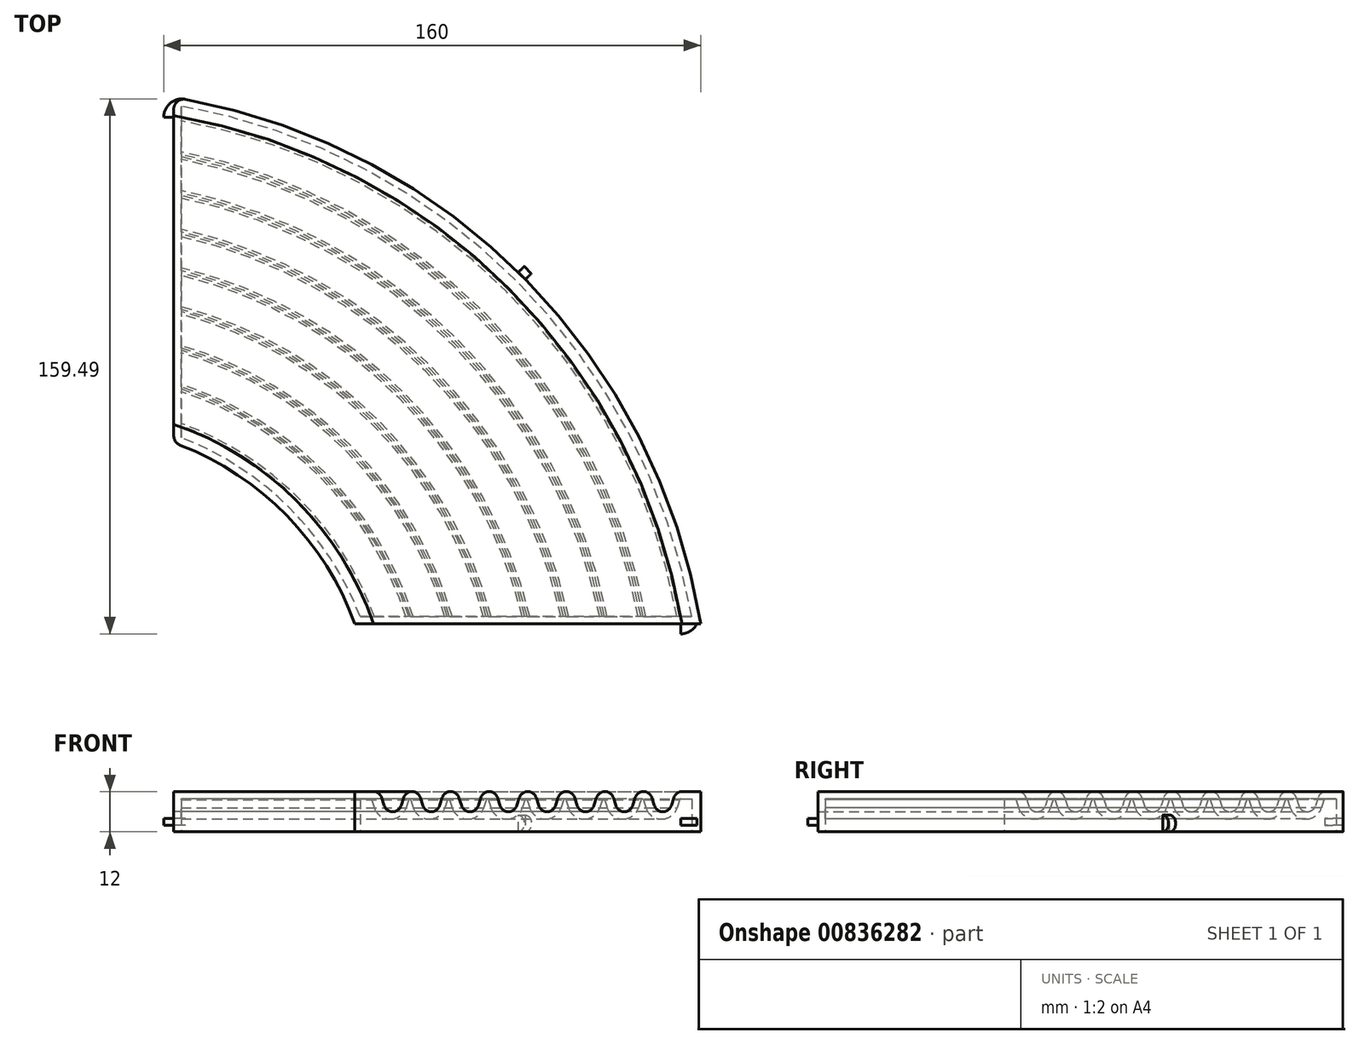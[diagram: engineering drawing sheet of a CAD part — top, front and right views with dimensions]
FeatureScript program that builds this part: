
annotation { "Feature Type Name" : "Feature", "Feature Type Description" : "" }
export const myFeature = defineFeature(function(context is Context, id is Id, definition is map)
    precondition{}
    {
        {
            var Q0;
            Q0=qCreatedBy(makeId("Right.planeOp"),FACE);
            cPlane(context, id + "F0", {"entities" : qUnion([Q0]), "cplaneType" : CPlaneType.OFFSET, "offset" : 31 * mm, "oppositeDirection" : true, "width" : 150 * mm, "height" : 150 * mm});
        }
        {
            var Q0;
            Q0=qCreatedBy(id+"F0.planeOp",FACE);
            var sketch = newSketch(context, id + "F1", { "sketchPlane" : qUnion([Q0])});
            skLineSegment(sketch, "E0", {"start": v(-31, 47.21) * mm, "end": v(-31, -48.38) * mm, "construction": true});
            skSolve(sketch);
        }
        {
            var Q0;
            Q0=qCreatedBy(makeId("Front.planeOp"),FACE);
            var sketch = newSketch(context, id + "F2", { "sketchPlane" : qUnion([Q0])});
            skLineSegment(sketch, "E1", {"start": v(0, 0) * mm, "end": v(54, 0) * mm, "construction": true});
            skLineSegment(sketch, "E2", {"start": v(54, 0) * mm, "end": v(54, 12) * mm});
            skLineSegment(sketch, "E3", {"start": v(54, 12) * mm, "end": v(59.5, 12) * mm});
            skLineSegment(sketch, "E4", {"start": v(59.5, 12) * mm, "end": v(71, 12) * mm, "construction": true});
            skLineSegment(sketch, "E5", {"start": v(65.25, 12) * mm, "end": v(65.25, 6) * mm, "construction": true});
            skLineSegment(sketch, "E6", {"start": v(151.5, 12) * mm, "end": v(157, 12) * mm});
            skLineSegment(sketch, "E7", {"start": v(157, 12) * mm, "end": v(157, 0) * mm});
            skLineSegment(sketch, "E8", {"start": v(157, 0) * mm, "end": v(54, 0) * mm});
            skLineSegment(sketch, "E9", {"start": v(0, 0) * mm, "end": v(0, 12) * mm, "construction": true});
            skLineSegment(sketch, "E10", {"start": v(65.25, 6) * mm, "end": v(71, 6) * mm, "construction": true});
            skArc(sketch, "E11", {"start": v(61.99, 10.19) * mm, "mid": v(61.04, 11.5) * mm, "end": v(59.5, 12) * mm});
            skLineSegment(sketch, "E12", {"start": v(61.99, 10.19) * mm, "end": v(62.76, 7.81) * mm});
            skArc(sketch, "E13", {"start": v(62.76, 7.81) * mm, "mid": v(63.71, 6.5) * mm, "end": v(65.25, 6) * mm});
            skLineSegment(sketch, "E14.MirrorCS", {"start": v(68.51, 10.19) * mm, "end": v(67.74, 7.81) * mm});
            skArc(sketch, "E15.MirrorCS", {"start": v(68.51, 10.19) * mm, "mid": v(69.46, 11.5) * mm, "end": v(71, 12) * mm});
            skArc(sketch, "E16.MirrorCS", {"start": v(67.74, 7.81) * mm, "mid": v(66.79, 6.5) * mm, "end": v(65.25, 6) * mm});
            skLineSegment(sketch, "E17.direction1", {"start": v(59.5, 9.38) * mm, "end": v(71, 9.38) * mm, "construction": true});
            skArc(sketch, "E18.1.0.0", {"start": v(73.49, 10.19) * mm, "mid": v(72.54, 11.5) * mm, "end": v(71, 12) * mm});
            skLineSegment(sketch, "E18.1.0.1", {"start": v(73.49, 10.19) * mm, "end": v(74.26, 7.81) * mm});
            skArc(sketch, "E18.1.0.2", {"start": v(74.26, 7.81) * mm, "mid": v(75.21, 6.5) * mm, "end": v(76.75, 6) * mm});
            skArc(sketch, "E18.1.0.3", {"start": v(79.24, 7.81) * mm, "mid": v(78.29, 6.5) * mm, "end": v(76.75, 6) * mm});
            skLineSegment(sketch, "E18.1.0.4", {"start": v(80.01, 10.19) * mm, "end": v(79.24, 7.81) * mm});
            skArc(sketch, "E18.1.0.5", {"start": v(80.01, 10.19) * mm, "mid": v(80.96, 11.5) * mm, "end": v(82.5, 12) * mm});
            skArc(sketch, "E18.2.0.0", {"start": v(84.99, 10.19) * mm, "mid": v(84.04, 11.5) * mm, "end": v(82.5, 12) * mm});
            skLineSegment(sketch, "E18.2.0.1", {"start": v(84.99, 10.19) * mm, "end": v(85.76, 7.81) * mm});
            skArc(sketch, "E18.2.0.2", {"start": v(85.76, 7.81) * mm, "mid": v(86.71, 6.5) * mm, "end": v(88.25, 6) * mm});
            skArc(sketch, "E18.2.0.3", {"start": v(90.74, 7.81) * mm, "mid": v(89.79, 6.5) * mm, "end": v(88.25, 6) * mm});
            skLineSegment(sketch, "E18.2.0.4", {"start": v(91.51, 10.19) * mm, "end": v(90.74, 7.81) * mm});
            skArc(sketch, "E18.2.0.5", {"start": v(91.51, 10.19) * mm, "mid": v(92.46, 11.5) * mm, "end": v(94, 12) * mm});
            skArc(sketch, "E18.3.0.0", {"start": v(96.49, 10.19) * mm, "mid": v(95.54, 11.5) * mm, "end": v(94, 12) * mm});
            skLineSegment(sketch, "E18.3.0.1", {"start": v(96.49, 10.19) * mm, "end": v(97.26, 7.81) * mm});
            skArc(sketch, "E18.3.0.2", {"start": v(97.26, 7.81) * mm, "mid": v(98.21, 6.5) * mm, "end": v(99.75, 6) * mm});
            skArc(sketch, "E18.3.0.3", {"start": v(102.24, 7.81) * mm, "mid": v(101.29, 6.5) * mm, "end": v(99.75, 6) * mm});
            skLineSegment(sketch, "E18.3.0.4", {"start": v(103.01, 10.19) * mm, "end": v(102.24, 7.81) * mm});
            skArc(sketch, "E18.3.0.5", {"start": v(103.01, 10.19) * mm, "mid": v(103.96, 11.5) * mm, "end": v(105.5, 12) * mm});
            skArc(sketch, "E18.4.0.0", {"start": v(107.99, 10.19) * mm, "mid": v(107.04, 11.5) * mm, "end": v(105.5, 12) * mm});
            skLineSegment(sketch, "E18.4.0.1", {"start": v(107.99, 10.19) * mm, "end": v(108.76, 7.81) * mm});
            skArc(sketch, "E18.4.0.2", {"start": v(108.76, 7.81) * mm, "mid": v(109.71, 6.5) * mm, "end": v(111.25, 6) * mm});
            skArc(sketch, "E18.4.0.3", {"start": v(113.74, 7.81) * mm, "mid": v(112.79, 6.5) * mm, "end": v(111.25, 6) * mm});
            skLineSegment(sketch, "E18.4.0.4", {"start": v(114.51, 10.19) * mm, "end": v(113.74, 7.81) * mm});
            skArc(sketch, "E18.4.0.5", {"start": v(114.51, 10.19) * mm, "mid": v(115.46, 11.5) * mm, "end": v(117, 12) * mm});
            skArc(sketch, "E18.5.0.0", {"start": v(119.49, 10.19) * mm, "mid": v(118.54, 11.5) * mm, "end": v(117, 12) * mm});
            skLineSegment(sketch, "E18.5.0.1", {"start": v(119.49, 10.19) * mm, "end": v(120.26, 7.81) * mm});
            skArc(sketch, "E18.5.0.2", {"start": v(120.26, 7.81) * mm, "mid": v(121.21, 6.5) * mm, "end": v(122.75, 6) * mm});
            skArc(sketch, "E18.5.0.3", {"start": v(125.24, 7.81) * mm, "mid": v(124.29, 6.5) * mm, "end": v(122.75, 6) * mm});
            skLineSegment(sketch, "E18.5.0.4", {"start": v(126.01, 10.19) * mm, "end": v(125.24, 7.81) * mm});
            skArc(sketch, "E18.5.0.5", {"start": v(126.01, 10.19) * mm, "mid": v(126.96, 11.5) * mm, "end": v(128.5, 12) * mm});
            skArc(sketch, "E18.6.0.0", {"start": v(130.99, 10.19) * mm, "mid": v(130.04, 11.5) * mm, "end": v(128.5, 12) * mm});
            skLineSegment(sketch, "E18.6.0.1", {"start": v(130.99, 10.19) * mm, "end": v(131.76, 7.81) * mm});
            skArc(sketch, "E18.6.0.2", {"start": v(131.76, 7.81) * mm, "mid": v(132.71, 6.5) * mm, "end": v(134.25, 6) * mm});
            skArc(sketch, "E18.6.0.3", {"start": v(136.74, 7.81) * mm, "mid": v(135.79, 6.5) * mm, "end": v(134.25, 6) * mm});
            skLineSegment(sketch, "E18.6.0.4", {"start": v(137.51, 10.19) * mm, "end": v(136.74, 7.81) * mm});
            skArc(sketch, "E18.6.0.5", {"start": v(137.51, 10.19) * mm, "mid": v(138.46, 11.5) * mm, "end": v(140, 12) * mm});
            skArc(sketch, "E18.7.0.0", {"start": v(142.49, 10.19) * mm, "mid": v(141.54, 11.5) * mm, "end": v(140, 12) * mm});
            skLineSegment(sketch, "E18.7.0.1", {"start": v(142.49, 10.19) * mm, "end": v(143.26, 7.81) * mm});
            skArc(sketch, "E18.7.0.2", {"start": v(143.26, 7.81) * mm, "mid": v(144.21, 6.5) * mm, "end": v(145.75, 6) * mm});
            skArc(sketch, "E18.7.0.3", {"start": v(148.24, 7.81) * mm, "mid": v(147.29, 6.5) * mm, "end": v(145.75, 6) * mm});
            skLineSegment(sketch, "E18.7.0.4", {"start": v(149.01, 10.19) * mm, "end": v(148.24, 7.81) * mm});
            skArc(sketch, "E18.7.0.5", {"start": v(149.01, 10.19) * mm, "mid": v(149.96, 11.5) * mm, "end": v(151.5, 12) * mm});
            skSolve(sketch);
        }
        {
            var Q0;
            Q0=makeQuery(id+"F2.imprint","IMPRINT",FACE,{"disambiguationData":[TD([[makeQuery(id+"F2.imprint","IMPRINT",EDGE,{"derivedFrom":sQuery(id+"F2.wireOp",EDGE,"E2")}),-1.0]])]});
            var Q1;
            Q1=sQuery(id+"F1.wireOp",EDGE,"E0");
            revolve(context, id + "F3", {"surfaceOperationType" : NewSurfaceOperationType.NEW, "entities" : qUnion([Q0]), "axis" : qUnion([Q1]), "revolveType" : RevolveType.ONE_DIRECTION, "oppositeDirection" : true, "angle" : 90 * degree});
        }
        {
            var Q0;
            Q0=qCreatedBy(makeId("Top.planeOp"),FACE);
            var sketch = newSketch(context, id + "F4", { "sketchPlane" : qUnion([Q0])});
            skLineSegment(sketch, "E19.bottom", {"start": v(0, 0) * mm, "end": v(-68.6, 0) * mm});
            skLineSegment(sketch, "E19.top", {"start": v(0, 163.62) * mm, "end": v(-68.6, 163.62) * mm});
            skLineSegment(sketch, "E19.left", {"start": v(0, 0) * mm, "end": v(0, 163.62) * mm});
            skLineSegment(sketch, "E19.right", {"start": v(-68.6, 0) * mm, "end": v(-68.6, 163.62) * mm});
            skLineSegment(sketch, "E20", {"start": v(0, 0) * mm, "end": v(103.73, 103.73) * mm, "construction": true});
            skSolve(sketch);
        }
        {
            var Q0;
            Q0=makeQuery(id+"F3.opRevolve","SWEPT_FACE",FACE,{"disambiguationData":[OSD([sQuery(id+"F2.wireOp",EDGE,"E8")])]});
            var Q1;
            Q1=makeQuery(id+"F3.opRevolve","SWEPT_BODY",BODY,{"disambiguationData":[OSD([sQuery(id+"F2.wireOp",EDGE,"E2"),sQuery(id+"F2.wireOp",EDGE,"E3"),sQuery(id+"F2.wireOp",EDGE,"E6"),sQuery(id+"F2.wireOp",EDGE,"E7"),sQuery(id+"F2.wireOp",EDGE,"E8"),sQuery(id+"F2.wireOp",EDGE,"E11"),sQuery(id+"F2.wireOp",EDGE,"E12"),sQuery(id+"F2.wireOp",EDGE,"E13"),sQuery(id+"F2.wireOp",EDGE,"E14.MirrorCS"),sQuery(id+"F2.wireOp",EDGE,"E15.MirrorCS"),sQuery(id+"F2.wireOp",EDGE,"E16.MirrorCS"),sQuery(id+"F2.wireOp",EDGE,"E17.1.0.0"),sQuery(id+"F2.wireOp",EDGE,"E17.1.0.1"),sQuery(id+"F2.wireOp",EDGE,"E17.1.0.2"),sQuery(id+"F2.wireOp",EDGE,"E17.1.0.3"),sQuery(id+"F2.wireOp",EDGE,"E17.1.0.4"),sQuery(id+"F2.wireOp",EDGE,"E17.1.0.5"),sQuery(id+"F2.wireOp",EDGE,"E17.2.0.0"),sQuery(id+"F2.wireOp",EDGE,"E17.2.0.1"),sQuery(id+"F2.wireOp",EDGE,"E17.2.0.2"),sQuery(id+"F2.wireOp",EDGE,"E17.2.0.3"),sQuery(id+"F2.wireOp",EDGE,"E17.2.0.4"),sQuery(id+"F2.wireOp",EDGE,"E17.2.0.5"),sQuery(id+"F2.wireOp",EDGE,"E17.3.0.0"),sQuery(id+"F2.wireOp",EDGE,"E17.3.0.1"),sQuery(id+"F2.wireOp",EDGE,"E17.3.0.2"),sQuery(id+"F2.wireOp",EDGE,"E17.3.0.3"),sQuery(id+"F2.wireOp",EDGE,"E17.3.0.4"),sQuery(id+"F2.wireOp",EDGE,"E17.3.0.5"),sQuery(id+"F2.wireOp",EDGE,"E17.4.0.0"),sQuery(id+"F2.wireOp",EDGE,"E17.4.0.1"),sQuery(id+"F2.wireOp",EDGE,"E17.4.0.2"),sQuery(id+"F2.wireOp",EDGE,"E17.4.0.3"),sQuery(id+"F2.wireOp",EDGE,"E17.4.0.4"),sQuery(id+"F2.wireOp",EDGE,"E17.4.0.5"),sQuery(id+"F2.wireOp",EDGE,"E17.5.0.0"),sQuery(id+"F2.wireOp",EDGE,"E17.5.0.1"),sQuery(id+"F2.wireOp",EDGE,"E17.5.0.2"),sQuery(id+"F2.wireOp",EDGE,"E17.5.0.3"),sQuery(id+"F2.wireOp",EDGE,"E17.5.0.4"),sQuery(id+"F2.wireOp",EDGE,"E17.5.0.5"),sQuery(id+"F2.wireOp",EDGE,"E17.6.0.0"),sQuery(id+"F2.wireOp",EDGE,"E17.6.0.1"),sQuery(id+"F2.wireOp",EDGE,"E17.6.0.2"),sQuery(id+"F2.wireOp",EDGE,"E17.6.0.3"),sQuery(id+"F2.wireOp",EDGE,"E17.6.0.4"),sQuery(id+"F2.wireOp",EDGE,"E17.6.0.5"),sQuery(id+"F2.wireOp",EDGE,"E17.7.0.0"),sQuery(id+"F2.wireOp",EDGE,"E17.7.0.1"),sQuery(id+"F2.wireOp",EDGE,"E17.7.0.2"),sQuery(id+"F2.wireOp",EDGE,"E17.7.0.3"),sQuery(id+"F2.wireOp",EDGE,"E17.7.0.4"),sQuery(id+"F2.wireOp",EDGE,"E17.7.0.5")])]});
            shell(context, id + "F5", {"entities" : qUnion([Q0]), "parts" : qUnion([Q1]), "thickness" : 2.2 * mm});
        }
        {
            var Q0;
            Q0 = qSketchRegion(id + "F4", true);
            extrude(context, id + "F6", {"entities" : qUnion([Q0]), "operationType" : NewBodyOperationType.REMOVE, "depth" : 25 * mm, "offsetDistance" : 25 * mm});
        }
        {
            var Q0;
            Q0=makeQuery(id+"F3.opRevolve","SWEPT_FACE",FACE,{"disambiguationData":[OSD([sQuery(id+"F2.wireOp",EDGE,"E8")])]});
            var sketch = newSketch(context, id + "F7", { "sketchPlane" : qUnion([Q0])});
            skLineSegment(sketch, "E21", {"start": v(0, -56.34) * mm, "end": v(0, -154.77) * mm});
            skLineSegment(sketch, "E22", {"start": v(2.2, -154.39) * mm, "end": v(2.2, -55.53) * mm});
            skArc(sketch, "E23.0", {"start": v(0, -154.77) * mm, "mid": v(1.1, -154.58) * mm, "end": v(2.2, -154.39) * mm});
            skPoint(sketch, "E24.orphan", {"position": v(154.39, -2.2) * mm});
            skArc(sketch, "E25.0", {"start": v(0, -56.34) * mm, "mid": v(1.1, -55.94) * mm, "end": v(2.2, -55.53) * mm});
            skPoint(sketch, "E26.orphan", {"position": v(55.53, -2.2) * mm});
            skSolve(sketch);
        }
        {
            var Q0;
            Q0 = qSketchRegion(id + "F7", true);
            extrude(context, id + "F8", {"entities" : qUnion([Q0]), "operationType" : NewBodyOperationType.ADD, "endBound" : BoundingType.UP_TO_NEXT, "oppositeDirection" : true, "depth" : 25 * mm, "offsetDistance" : 25 * mm});
        }
        {
            var Q0;
            Q0=makeQuery(id+"F3.opRevolve","CAP_EDGE",EDGE,{"disambiguationData":[OSD([sQuery(id+"F2.wireOp",EDGE,"E2")]),OD(0.0)],"isStart":false});
            var Q1;
            Q1=makeQuery(id+"F3.opRevolve","CAP_EDGE",EDGE,{"disambiguationData":[OSD([sQuery(id+"F2.wireOp",EDGE,"E7")]),OD(0.0)],"isStart":false});
            var Q2;
            Q2=makeQuery(id+"F6.boolean.opBoolean","INTERSECT",EDGE,{"derivedFrom":[makeQuery(id+"F3.opRevolve","SWEPT_FACE",FACE,{"disambiguationData":[OSD([sQuery(id+"F2.wireOp",EDGE,"E2")])]}),makeQuery(id+"F6.opExtrude","SWEPT_FACE",FACE,{"disambiguationData":[OSD([sQuery(id+"F4.wireOp",EDGE,"E19.left")])]})]});
            var Q3;
            Q3=makeQuery(id+"F6.boolean.opBoolean","INTERSECT",EDGE,{"derivedFrom":[makeQuery(id+"F3.opRevolve","SWEPT_FACE",FACE,{"disambiguationData":[OSD([sQuery(id+"F2.wireOp",EDGE,"E7")])]}),makeQuery(id+"F6.opExtrude","SWEPT_FACE",FACE,{"disambiguationData":[OSD([sQuery(id+"F4.wireOp",EDGE,"E19.left")])]})]});
            fillet(context, id + "F9", {"entities" : qUnion([Q0, Q1, Q2, Q3]), "radius" : 3 * mm, "tangentPropagation" : true, "allowEdgeOverflow" : false});
        }
        {
            var Q0;
            Q0=qCreatedBy(makeId("Top.planeOp"),FACE);
            cPlane(context, id + "F10", {"entities" : qUnion([Q0]), "cplaneType" : CPlaneType.OFFSET, "offset" : 2 * mm, "width" : 150 * mm, "height" : 150 * mm});
        }
        {
            var Q0;
            Q0=qCreatedBy(id+"F10.planeOp",FACE);
            var sketch = newSketch(context, id + "F11", { "sketchPlane" : qUnion([Q0])});
            skLineSegment(sketch, "E27", {"start": v(151.03, 0) * mm, "end": v(151.03, -3) * mm});
            skArc(sketch, "E28", {"start": v(151.03, -3) * mm, "mid": v(155.23, -1.03) * mm, "end": v(156.4, 3.45) * mm});
            skLineSegment(sketch, "E29", {"start": v(156.38, 3.54) * mm, "end": v(156.4, 3.45) * mm});
            skArc(sketch, "E30", {"start": v(153.43, 0) * mm, "mid": v(155.74, 1.08) * mm, "end": v(156.38, 3.54) * mm});
            skLineSegment(sketch, "E31", {"start": v(151.03, 0) * mm, "end": v(153.43, 0) * mm});
            skPoint(sketch, "E32.center", {"position": v(0, 0) * mm});
            skLineSegment(sketch, "E32.anchor1", {"start": v(0, 0) * mm, "end": v(151.03, 0) * mm, "construction": true});
            skPoint(sketch, "E33.center", {"position": v(-0.97, 0) * mm});
            skLineSegment(sketch, "E33.anchor1", {"start": v(-0.97, 0) * mm, "end": v(151.03, 0) * mm, "construction": true});
            skLineSegment(sketch, "E34.1.3", {"start": v(0, 151.03) * mm, "end": v(0, 153.43) * mm});
            skLineSegment(sketch, "E34.1.4", {"start": v(-3.54, 156.38) * mm, "end": v(-3.45, 156.4) * mm});
            skLineSegment(sketch, "E34.anchor2", {"start": v(0, 0) * mm, "end": v(0, 151.03) * mm, "construction": true});
            skLineSegment(sketch, "E35.MirrorCS", {"start": v(3.54, 156.38) * mm, "end": v(3.45, 156.4) * mm});
            skLineSegment(sketch, "E36.MirrorCS", {"start": v(0, 151.03) * mm, "end": v(-3, 151.03) * mm});
            skArc(sketch, "E37.MirrorCS", {"start": v(-3, 151.03) * mm, "mid": v(-1.03, 155.23) * mm, "end": v(3.45, 156.4) * mm});
            skArc(sketch, "E38.MirrorCS", {"start": v(0, 153.43) * mm, "mid": v(1.08, 155.74) * mm, "end": v(3.54, 156.38) * mm});
            skSolve(sketch);
        }
        {
            var Q0;
            Q0 = qSketchRegion(id + "F11", true);
            extrude(context, id + "F12", {"entities" : qUnion([Q0]), "operationType" : NewBodyOperationType.ADD, "depth" : 2 * mm, "offsetDistance" : 25 * mm});
        }
        {
            var Q0;
            Q0=qCreatedBy(makeId("Right.planeOp"),FACE);
            var Q1;
            Q1=sQuery(id+"F4.wireOp",EDGE,"E20");
            cPlane(context, id + "F13", {"entities" : qUnion([Q0, Q1]), "cplaneType" : CPlaneType.LINE_ANGLE, "offset" : 25 * mm, "angle" : 0 * degree, "width" : 150 * mm, "height" : 150 * mm});
        }
        {
            var Q0;
            Q0=qCreatedBy(id+"F13.planeOp",FACE);
            var sketch = newSketch(context, id + "F14", { "sketchPlane" : qUnion([Q0])});
            skCircle(sketch, "E39", {"center": v(-146.7, 2.5) * mm, "radius": 2.5 * mm});
            skLineSegment(sketch, "E40", {"start": v(-146.7, 0) * mm, "end": v(-146.7, 12) * mm});
            skSolve(sketch);
        }
        {
            var Q0;
            {var subQ0=sQuery(id+"F14.wireOp",EDGE,"E40");var subQ1=sQuery(id+"F14.wireOp",EDGE,"E39");var subQ2=makeQuery(id+"F14.imprint","INTERSECT",VERTEX,{"disambiguationData":[OD(0.0)],"derivedFrom":[subQ1,subQ0]});Q0=makeQuery(id+"F14.imprint","IMPRINT",FACE,{"disambiguationData":[TD([[makeQuery(id+"F14.imprint","IMPRINT",EDGE,{"disambiguationData":[TD([[subQ2,1.0]])],"derivedFrom":subQ1}),1.0]])]});}
            extrude(context, id + "F15", {"entities" : qUnion([Q0]), "operationType" : NewBodyOperationType.ADD, "depth" : 3 * mm, "offsetDistance" : 25 * mm, "symmetric" : true});
        }
    });
